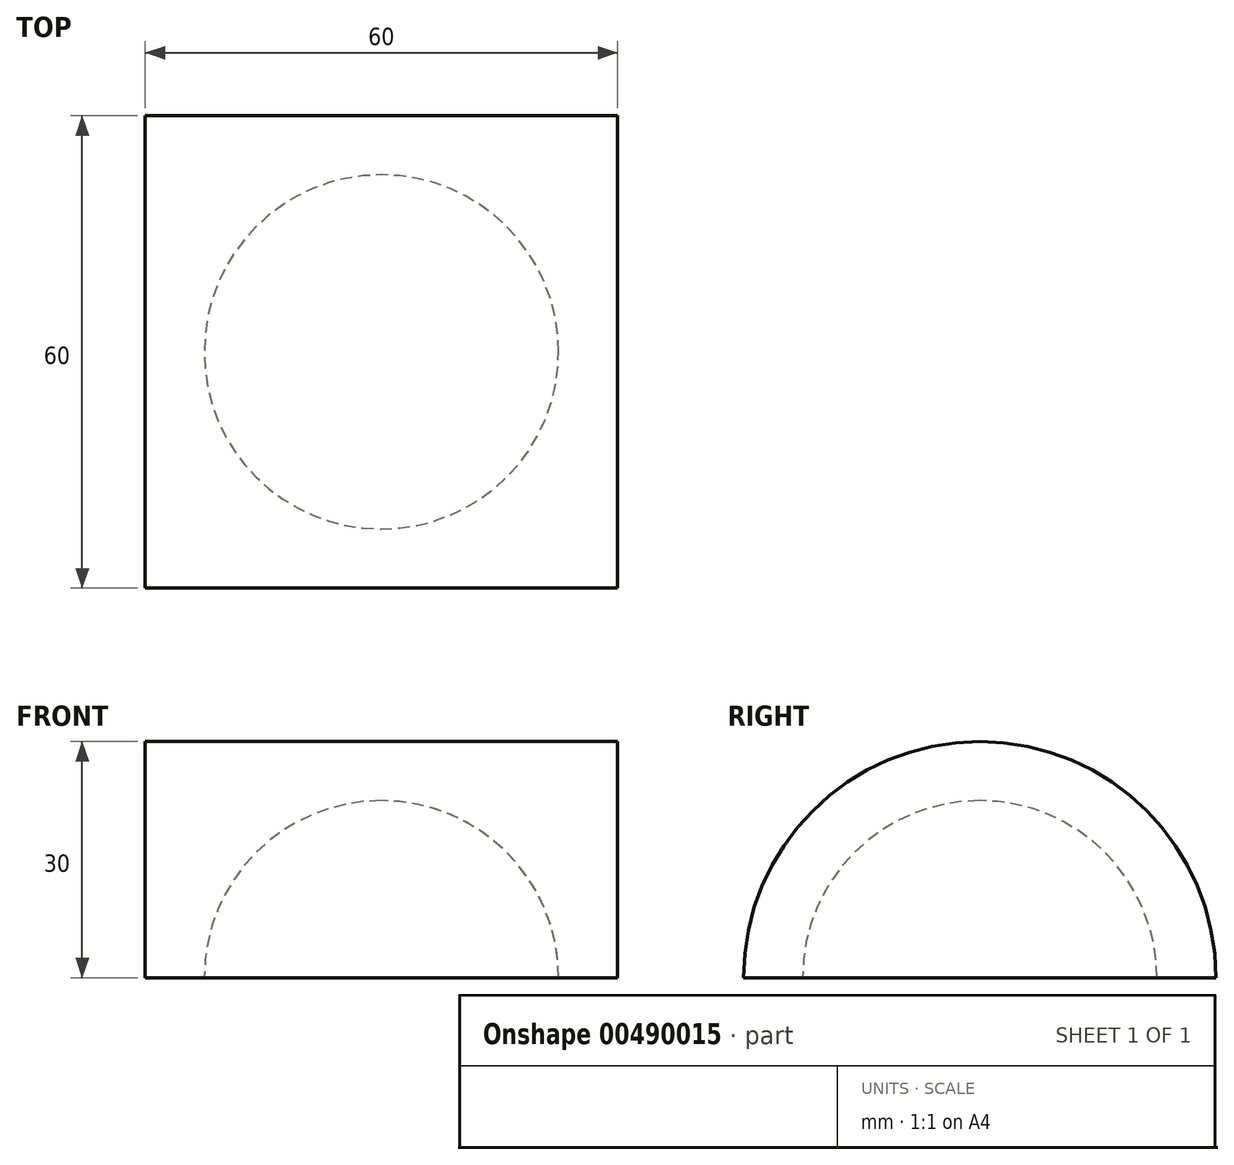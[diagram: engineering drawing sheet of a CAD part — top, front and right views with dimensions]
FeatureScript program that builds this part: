
annotation { "Feature Type Name" : "Feature", "Feature Type Description" : "" }
export const myFeature = defineFeature(function(context is Context, id is Id, definition is map)
    precondition{}
    {
        {
            var Q0;
            Q0=qCreatedBy(makeId("Top.planeOp"),FACE);
            var sketch = newSketch(context, id + "F0", { "sketchPlane" : qUnion([Q0])});
            skLineSegment(sketch, "E0.bottom", {"start": v(30, 30) * mm, "end": v(-30, 30) * mm});
            skLineSegment(sketch, "E0.top", {"start": v(30, -30) * mm, "end": v(-30, -30) * mm});
            skLineSegment(sketch, "E0.left", {"start": v(30, 30) * mm, "end": v(30, -30) * mm});
            skLineSegment(sketch, "E0.right", {"start": v(-30, 30) * mm, "end": v(-30, -30) * mm});
            skPoint(sketch, "E0.middle", {"position": v(0, 0) * mm});
            skCircle(sketch, "E1", {"center": v(0, 0) * mm, "radius": 22.5 * mm});
            skSolve(sketch);
        }
        {
            var Q0;
            Q0=makeQuery(id+"F0.imprint","IMPRINT",FACE,{"disambiguationData":[TD([[makeQuery(id+"F0.imprint","IMPRINT",EDGE,{"derivedFrom":sQuery(id+"F0.wireOp",EDGE,"E0.bottom")}),1.0]])]});
            var Q1;
            Q1=makeQuery(id+"F0.imprint","IMPRINT",FACE,{"disambiguationData":[TD([[makeQuery(id+"F0.imprint","IMPRINT",EDGE,{"derivedFrom":sQuery(id+"F0.wireOp",EDGE,"GQa6SJnh-tApy-H6hX-5Uq1-EjaBYNNtFakJ")}),1.0]])]});
            var Q2;
            Q2=makeQuery(id+"F0.imprint","IMPRINT",FACE,{"disambiguationData":[TD([[makeQuery(id+"F0.imprint","IMPRINT",EDGE,{"derivedFrom":sQuery(id+"F0.wireOp",EDGE,"E1")}),1.0]])]});
            extrude(context, id + "F1", {"entities" : qUnion([Q0, Q1, Q2]), "depth" : 30 * mm, "offsetDistance" : 25 * mm});
        }
        {
            var Q0;
            Q0=makeQuery(id+"F0.imprint","IMPRINT",FACE,{"disambiguationData":[TD([[makeQuery(id+"F0.imprint","IMPRINT",EDGE,{"derivedFrom":sQuery(id+"F0.wireOp",EDGE,"E1")}),1.0]])]});
            extrude(context, id + "F2", {"entities" : qUnion([Q0]), "operationType" : NewBodyOperationType.REMOVE, "depth" : 22.5 * mm, "offsetDistance" : 25 * mm});
        }
        {
            var Q0;
            Q0=makeQuery(id+"F2.boolean.opBoolean","COPY",EDGE,{"derivedFrom":makeQuery(id+"F2.opExtrude","CAP_EDGE",EDGE,{"disambiguationData":[OSD([sQuery(id+"F0.wireOp",EDGE,"E1")])],"isStart":false})});
            fillet(context, id + "F3", {"entities" : qUnion([Q0]), "radius" : 22.5 * mm, "tangentPropagation" : true, "allowEdgeOverflow" : false});
        }
        {
            var Q0;
            Q0=makeQuery(id+"F1.opExtrude","CAP_EDGE",EDGE,{"disambiguationData":[OSD([sQuery(id+"F0.wireOp",EDGE,"E0.top")])],"isStart":false});
            var Q1;
            Q1=makeQuery(id+"F1.opExtrude","CAP_EDGE",EDGE,{"disambiguationData":[OSD([sQuery(id+"F0.wireOp",EDGE,"E0.bottom")])],"isStart":false});
            fillet(context, id + "F4", {"entities" : qUnion([Q0, Q1]), "radius" : 30 * mm, "tangentPropagation" : true, "allowEdgeOverflow" : false});
        }
    });
